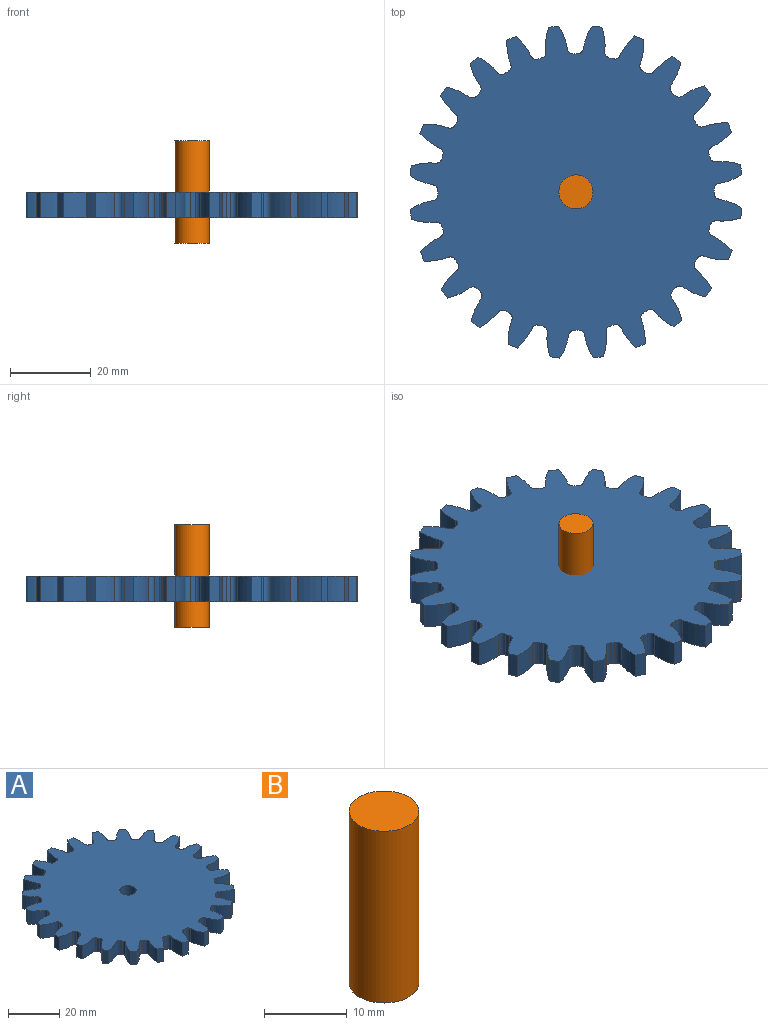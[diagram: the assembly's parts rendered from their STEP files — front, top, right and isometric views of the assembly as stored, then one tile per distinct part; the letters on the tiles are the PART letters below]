
ASSEMBLY  parts=2 mates=1
PART A: 147 faces, bbox 82.5x82.5x6.4 mm
  f0: cylinder r=3.17mm len=6.35mm, axis (0,0,1), area 126.7mm2, adj f39,f40
  f1: cylinder r=1.31mm len=6.35mm, axis (0,0,-1), area 11.8mm2, adj f39,f40,f143,f146
  f2: cylinder r=1.31mm len=6.35mm, axis (0,0,-1), area 11.8mm2, adj f39,f40,f139,f141
  f3: cylinder r=1.31mm len=6.35mm, axis (0,0,-1), area 11.8mm2, adj f39,f40,f135,f137
  f4: cylinder r=1.31mm len=6.35mm, axis (0,0,-1), area 11.8mm2, adj f39,f40,f131,f133
  f5: cylinder r=1.31mm len=6.35mm, axis (0,0,-1), area 11.8mm2, adj f39,f40,f127,f129
  f6: cylinder r=15.12mm len=6.35mm, axis (0,0,-1), area 39.4mm2, adj f21,f39,f40,f120
  f7: cylinder r=15.12mm len=6.35mm, axis (0,0,-1), area 39.4mm2, adj f31,f39,f40,f74
  f8: cylinder r=15.12mm len=6.35mm, axis (0,0,-1), area 39.4mm2, adj f32,f39,f40,f70
  f9: cylinder r=1.31mm len=6.35mm, axis (0,0,-1), area 11.8mm2, adj f39,f40,f62,f64
  f10: cylinder r=1.31mm len=6.35mm, axis (0,0,-1), area 11.8mm2, adj f39,f40,f58,f60
  f11: cylinder r=1.31mm len=6.35mm, axis (0,0,-1), area 11.8mm2, adj f39,f40,f54,f56
  f12: cylinder r=1.31mm len=6.35mm, axis (0,0,-1), area 11.8mm2, adj f39,f40,f50,f52
  f13: cylinder r=1.31mm len=6.35mm, axis (0,0,-1), area 11.8mm2, adj f39,f40,f47,f48
  f14: cylinder r=1.31mm len=6.35mm, axis (0,0,-1), area 11.8mm2, adj f39,f40,f41,f44
  f15: cylinder r=41.27mm len=6.35mm, axis (0,0,-1), area 15.7mm2, adj f39,f40,f142,f143
  f16: cylinder r=41.27mm len=6.35mm, axis (0,0,-1), area 15.7mm2, adj f39,f40,f41,f144
  f17: cylinder r=41.27mm len=6.35mm, axis (0,0,-1), area 15.7mm2, adj f39,f40,f138,f141
  f18: cylinder r=41.27mm len=6.35mm, axis (0,0,-1), area 15.7mm2, adj f39,f40,f134,f137
  f19: cylinder r=41.27mm len=6.35mm, axis (0,0,-1), area 15.7mm2, adj f39,f40,f130,f133
  f20: cylinder r=41.27mm len=6.35mm, axis (0,0,-1), area 15.7mm2, adj f39,f40,f126,f129
  f21: cylinder r=41.27mm len=6.35mm, axis (0,0,-1), area 15.7mm2, adj f6,f39,f40,f125
  f22: cylinder r=41.27mm len=6.35mm, axis (0,0,-1), area 15.7mm2, adj f39,f40,f117,f121
  f23: cylinder r=41.27mm len=6.35mm, axis (0,0,-1), area 15.7mm2, adj f39,f40,f112,f116
  f24: cylinder r=41.27mm len=6.35mm, axis (0,0,-1), area 15.7mm2, adj f39,f40,f107,f111
  f25: cylinder r=41.27mm len=6.35mm, axis (0,0,-1), area 15.7mm2, adj f39,f40,f102,f106
  f26: cylinder r=41.27mm len=6.35mm, axis (0,0,-1), area 15.7mm2, adj f39,f40,f97,f101
  f27: cylinder r=41.27mm len=6.35mm, axis (0,0,-1), area 15.7mm2, adj f39,f40,f92,f96
  f28: cylinder r=41.27mm len=6.35mm, axis (0,0,-1), area 15.7mm2, adj f39,f40,f87,f91
  f29: cylinder r=41.27mm len=6.35mm, axis (0,0,-1), area 15.7mm2, adj f39,f40,f82,f86
  f30: cylinder r=41.27mm len=6.35mm, axis (0,0,-1), area 15.7mm2, adj f39,f40,f77,f81
  f31: cylinder r=41.27mm len=6.35mm, axis (0,0,-1), area 15.7mm2, adj f7,f39,f40,f73
  f32: cylinder r=41.27mm len=6.35mm, axis (0,0,-1), area 15.7mm2, adj f8,f39,f40,f69
  f33: cylinder r=41.27mm len=6.35mm, axis (0,0,-1), area 15.7mm2, adj f39,f40,f64,f68
  f34: cylinder r=41.27mm len=6.35mm, axis (0,0,-1), area 15.7mm2, adj f39,f40,f60,f63
  f35: cylinder r=41.27mm len=6.35mm, axis (0,0,-1), area 15.7mm2, adj f39,f40,f56,f59
  f36: cylinder r=41.27mm len=6.35mm, axis (0,0,-1), area 15.7mm2, adj f39,f40,f52,f55
  f37: cylinder r=41.27mm len=6.35mm, axis (0,0,-1), area 15.7mm2, adj f39,f40,f48,f51
  f38: cylinder r=41.27mm len=6.35mm, axis (0,0,-1), area 15.7mm2, adj f39,f40,f42,f45
  f39: plane 82.53x82.53mm, normal (0,0,1), area 4433.5mm2, adj f0,f1,f2,f3,f4,f5,f6,f7
  f40: plane 82.53x82.53mm, normal (0,0,-1), area 4433.5mm2, adj f0,f1,f2,f3,f4,f5,f6,f7
  f41: cylinder r=15.12mm len=6.35mm, axis (0,0,-1), area 39.4mm2, adj f14,f16,f39,f40
  f42: cylinder r=15.12mm len=6.35mm, axis (0,0,-1), area 39.4mm2, adj f38,f39,f40,f43
  f43: cylinder r=1.31mm len=6.35mm, axis (0,0,-1), area 11.8mm2, adj f39,f40,f42,f44
  f44: cylinder r=34.24mm len=6.35mm, axis (0,0,-1), area 7.7mm2, adj f14,f39,f40,f43
  f45: cylinder r=15.12mm len=6.35mm, axis (0,0,-1), area 39.4mm2, adj f38,f39,f40,f46
  f46: cylinder r=1.31mm len=6.35mm, axis (0,0,-1), area 11.8mm2, adj f39,f40,f45,f47
  f47: cylinder r=34.24mm len=6.35mm, axis (0,0,-1), area 7.7mm2, adj f13,f39,f40,f46
  f48: cylinder r=15.12mm len=6.35mm, axis (0,0,-1), area 39.4mm2, adj f13,f37,f39,f40
  f49: cylinder r=1.31mm len=6.35mm, axis (0,0,-1), area 11.8mm2, adj f39,f40,f50,f51
  f50: cylinder r=34.24mm len=6.35mm, axis (0,0,-1), area 7.7mm2, adj f12,f39,f40,f49
  f51: cylinder r=15.12mm len=6.35mm, axis (0,0,-1), area 39.4mm2, adj f37,f39,f40,f49
  f52: cylinder r=15.12mm len=6.35mm, axis (0,0,-1), area 39.4mm2, adj f12,f36,f39,f40
  f53: cylinder r=1.31mm len=6.35mm, axis (0,0,-1), area 11.8mm2, adj f39,f40,f54,f55
  f54: cylinder r=34.24mm len=6.35mm, axis (0,0,-1), area 7.7mm2, adj f11,f39,f40,f53
  f55: cylinder r=15.12mm len=6.35mm, axis (0,0,-1), area 39.4mm2, adj f36,f39,f40,f53
  f56: cylinder r=15.12mm len=6.35mm, axis (0,0,-1), area 39.4mm2, adj f11,f35,f39,f40
  f57: cylinder r=1.31mm len=6.35mm, axis (0,0,-1), area 11.8mm2, adj f39,f40,f58,f59
  f58: cylinder r=34.24mm len=6.35mm, axis (0,0,-1), area 7.7mm2, adj f10,f39,f40,f57
  f59: cylinder r=15.12mm len=6.35mm, axis (0,0,-1), area 39.4mm2, adj f35,f39,f40,f57
  f60: cylinder r=15.12mm len=6.35mm, axis (0,0,-1), area 39.4mm2, adj f10,f34,f39,f40
  f61: cylinder r=1.31mm len=6.35mm, axis (0,0,-1), area 11.8mm2, adj f39,f40,f62,f63
  f62: cylinder r=34.24mm len=6.35mm, axis (0,0,-1), area 7.7mm2, adj f9,f39,f40,f61
  f63: cylinder r=15.12mm len=6.35mm, axis (0,0,-1), area 39.4mm2, adj f34,f39,f40,f61
  f64: cylinder r=15.12mm len=6.35mm, axis (0,0,-1), area 39.4mm2, adj f9,f33,f39,f40
  f65: cylinder r=1.31mm len=6.35mm, axis (0,0,-1), area 11.8mm2, adj f39,f40,f66,f68
  f66: cylinder r=34.24mm len=6.35mm, axis (0,0,-1), area 7.7mm2, adj f39,f40,f65,f67
  f67: cylinder r=1.31mm len=6.35mm, axis (0,0,-1), area 11.8mm2, adj f39,f40,f66,f69
  f68: cylinder r=15.12mm len=6.35mm, axis (0,0,-1), area 39.4mm2, adj f33,f39,f40,f65
  f69: cylinder r=15.12mm len=6.35mm, axis (0,0,-1), area 39.4mm2, adj f32,f39,f40,f67
  f70: cylinder r=1.31mm len=6.35mm, axis (0,0,-1), area 11.8mm2, adj f8,f39,f40,f71
  f71: cylinder r=34.24mm len=6.35mm, axis (0,0,-1), area 7.7mm2, adj f39,f40,f70,f72
  f72: cylinder r=1.31mm len=6.35mm, axis (0,0,-1), area 11.8mm2, adj f39,f40,f71,f73
  f73: cylinder r=15.12mm len=6.35mm, axis (0,0,-1), area 39.4mm2, adj f31,f39,f40,f72
  f74: cylinder r=1.31mm len=6.35mm, axis (0,0,-1), area 11.8mm2, adj f7,f39,f40,f75
  f75: cylinder r=34.24mm len=6.35mm, axis (0,0,-1), area 7.7mm2, adj f39,f40,f74,f76
  f76: cylinder r=1.31mm len=6.35mm, axis (0,0,-1), area 11.8mm2, adj f39,f40,f75,f77
  f77: cylinder r=15.12mm len=6.35mm, axis (0,0,-1), area 39.4mm2, adj f30,f39,f40,f76
  f78: cylinder r=1.31mm len=6.35mm, axis (0,0,-1), area 11.8mm2, adj f39,f40,f79,f81
  f79: cylinder r=34.24mm len=6.35mm, axis (0,0,-1), area 7.7mm2, adj f39,f40,f78,f80
  f80: cylinder r=1.31mm len=6.35mm, axis (0,0,-1), area 11.8mm2, adj f39,f40,f79,f82
  f81: cylinder r=15.12mm len=6.35mm, axis (0,0,-1), area 39.4mm2, adj f30,f39,f40,f78
  f82: cylinder r=15.12mm len=6.35mm, axis (0,0,-1), area 39.4mm2, adj f29,f39,f40,f80
  f83: cylinder r=1.31mm len=6.35mm, axis (0,0,-1), area 11.8mm2, adj f39,f40,f84,f86
  f84: cylinder r=34.24mm len=6.35mm, axis (0,0,-1), area 7.7mm2, adj f39,f40,f83,f85
  f85: cylinder r=1.31mm len=6.35mm, axis (0,0,-1), area 11.8mm2, adj f39,f40,f84,f87
  f86: cylinder r=15.12mm len=6.35mm, axis (0,0,-1), area 39.4mm2, adj f29,f39,f40,f83
  f87: cylinder r=15.12mm len=6.35mm, axis (0,0,-1), area 39.4mm2, adj f28,f39,f40,f85
  f88: cylinder r=1.31mm len=6.35mm, axis (0,0,-1), area 11.8mm2, adj f39,f40,f89,f91
  f89: cylinder r=34.24mm len=6.35mm, axis (0,0,-1), area 7.7mm2, adj f39,f40,f88,f90
  f90: cylinder r=1.31mm len=6.35mm, axis (0,0,-1), area 11.8mm2, adj f39,f40,f89,f92
  f91: cylinder r=15.12mm len=6.35mm, axis (0,0,-1), area 39.4mm2, adj f28,f39,f40,f88
  f92: cylinder r=15.12mm len=6.35mm, axis (0,0,-1), area 39.4mm2, adj f27,f39,f40,f90
  f93: cylinder r=1.31mm len=6.35mm, axis (0,0,-1), area 11.8mm2, adj f39,f40,f94,f96
  f94: cylinder r=34.24mm len=6.35mm, axis (0,0,-1), area 7.7mm2, adj f39,f40,f93,f95
  f95: cylinder r=1.31mm len=6.35mm, axis (0,0,-1), area 11.8mm2, adj f39,f40,f94,f97
  f96: cylinder r=15.12mm len=6.35mm, axis (0,0,-1), area 39.4mm2, adj f27,f39,f40,f93
  f97: cylinder r=15.12mm len=6.35mm, axis (0,0,-1), area 39.4mm2, adj f26,f39,f40,f95
  f98: cylinder r=1.31mm len=6.35mm, axis (0,0,-1), area 11.8mm2, adj f39,f40,f99,f101
  f99: cylinder r=34.24mm len=6.35mm, axis (0,0,-1), area 7.7mm2, adj f39,f40,f98,f100
  f100: cylinder r=1.31mm len=6.35mm, axis (0,0,-1), area 11.8mm2, adj f39,f40,f99,f102
  f101: cylinder r=15.12mm len=6.35mm, axis (0,0,-1), area 39.4mm2, adj f26,f39,f40,f98
  f102: cylinder r=15.12mm len=6.35mm, axis (0,0,-1), area 39.4mm2, adj f25,f39,f40,f100
  f103: cylinder r=1.31mm len=6.35mm, axis (0,0,-1), area 11.8mm2, adj f39,f40,f104,f106
  f104: cylinder r=34.24mm len=6.35mm, axis (0,0,-1), area 7.7mm2, adj f39,f40,f103,f105
  f105: cylinder r=1.31mm len=6.35mm, axis (0,0,-1), area 11.8mm2, adj f39,f40,f104,f107
  f106: cylinder r=15.12mm len=6.35mm, axis (0,0,-1), area 39.4mm2, adj f25,f39,f40,f103
  f107: cylinder r=15.12mm len=6.35mm, axis (0,0,-1), area 39.4mm2, adj f24,f39,f40,f105
  f108: cylinder r=1.31mm len=6.35mm, axis (0,0,-1), area 11.8mm2, adj f39,f40,f109,f111
  f109: cylinder r=34.24mm len=6.35mm, axis (0,0,-1), area 7.7mm2, adj f39,f40,f108,f110
  f110: cylinder r=1.31mm len=6.35mm, axis (0,0,-1), area 11.8mm2, adj f39,f40,f109,f112
  f111: cylinder r=15.12mm len=6.35mm, axis (0,0,-1), area 39.4mm2, adj f24,f39,f40,f108
  f112: cylinder r=15.12mm len=6.35mm, axis (0,0,-1), area 39.4mm2, adj f23,f39,f40,f110
  f113: cylinder r=1.31mm len=6.35mm, axis (0,0,-1), area 11.8mm2, adj f39,f40,f114,f116
  f114: cylinder r=34.24mm len=6.35mm, axis (0,0,-1), area 7.7mm2, adj f39,f40,f113,f115
  f115: cylinder r=1.31mm len=6.35mm, axis (0,0,-1), area 11.8mm2, adj f39,f40,f114,f117
  f116: cylinder r=15.12mm len=6.35mm, axis (0,0,-1), area 39.4mm2, adj f23,f39,f40,f113
  f117: cylinder r=15.12mm len=6.35mm, axis (0,0,-1), area 39.4mm2, adj f22,f39,f40,f115
  f118: cylinder r=1.31mm len=6.35mm, axis (0,0,-1), area 11.8mm2, adj f39,f40,f119,f121
  f119: cylinder r=34.24mm len=6.35mm, axis (0,0,-1), area 7.7mm2, adj f39,f40,f118,f120
  f120: cylinder r=1.31mm len=6.35mm, axis (0,0,-1), area 11.8mm2, adj f6,f39,f40,f119
  f121: cylinder r=15.12mm len=6.35mm, axis (0,0,-1), area 39.4mm2, adj f22,f39,f40,f118
  f122: cylinder r=1.31mm len=6.35mm, axis (0,0,-1), area 11.8mm2, adj f39,f40,f123,f125
  f123: cylinder r=34.24mm len=6.35mm, axis (0,0,-1), area 7.7mm2, adj f39,f40,f122,f124
  f124: cylinder r=1.31mm len=6.35mm, axis (0,0,-1), area 11.8mm2, adj f39,f40,f123,f126
  f125: cylinder r=15.12mm len=6.35mm, axis (0,0,-1), area 39.4mm2, adj f21,f39,f40,f122
  f126: cylinder r=15.12mm len=6.35mm, axis (0,0,-1), area 39.4mm2, adj f20,f39,f40,f124
  f127: cylinder r=34.24mm len=6.35mm, axis (0,0,-1), area 7.7mm2, adj f5,f39,f40,f128
  f128: cylinder r=1.31mm len=6.35mm, axis (0,0,-1), area 11.8mm2, adj f39,f40,f127,f130
  f129: cylinder r=15.12mm len=6.35mm, axis (0,0,-1), area 39.4mm2, adj f5,f20,f39,f40
  f130: cylinder r=15.12mm len=6.35mm, axis (0,0,-1), area 39.4mm2, adj f19,f39,f40,f128
  f131: cylinder r=34.24mm len=6.35mm, axis (0,0,-1), area 7.7mm2, adj f4,f39,f40,f132
  f132: cylinder r=1.31mm len=6.35mm, axis (0,0,-1), area 11.8mm2, adj f39,f40,f131,f134
  f133: cylinder r=15.12mm len=6.35mm, axis (0,0,-1), area 39.4mm2, adj f4,f19,f39,f40
  f134: cylinder r=15.12mm len=6.35mm, axis (0,0,-1), area 39.4mm2, adj f18,f39,f40,f132
  f135: cylinder r=34.24mm len=6.35mm, axis (0,0,-1), area 7.7mm2, adj f3,f39,f40,f136
  f136: cylinder r=1.31mm len=6.35mm, axis (0,0,-1), area 11.8mm2, adj f39,f40,f135,f138
  f137: cylinder r=15.12mm len=6.35mm, axis (0,0,-1), area 39.4mm2, adj f3,f18,f39,f40
  f138: cylinder r=15.12mm len=6.35mm, axis (0,0,-1), area 39.4mm2, adj f17,f39,f40,f136
  f139: cylinder r=34.24mm len=6.35mm, axis (0,0,-1), area 7.7mm2, adj f2,f39,f40,f140
  f140: cylinder r=1.31mm len=6.35mm, axis (0,0,-1), area 11.8mm2, adj f39,f40,f139,f142
  f141: cylinder r=15.12mm len=6.35mm, axis (0,0,-1), area 39.4mm2, adj f2,f17,f39,f40
  f142: cylinder r=15.12mm len=6.35mm, axis (0,0,-1), area 39.4mm2, adj f15,f39,f40,f140
  f143: cylinder r=15.12mm len=6.35mm, axis (0,0,-1), area 39.4mm2, adj f1,f15,f39,f40
  f144: cylinder r=15.12mm len=6.35mm, axis (0,0,-1), area 39.4mm2, adj f16,f39,f40,f145
  f145: cylinder r=1.31mm len=6.35mm, axis (0,0,-1), area 11.8mm2, adj f39,f40,f144,f146
  f146: cylinder r=34.24mm len=6.35mm, axis (0,0,-1), area 7.7mm2, adj f1,f39,f40,f145
PART B: 3 faces, bbox 8.4x8.4x25.4 mm
  f0: cylinder r=4.22mm len=25.4mm, axis (0,0,-1), area 673.2mm2, adj f1,f2
  f1: plane 8.44x8.44mm, normal (0,0,1), area 55.9mm2, adj f0
  f2: plane 8.44x8.44mm, normal (0,0,-1), area 55.9mm2, adj f0
PLACE A rot(axis=(0,0,-1),10.1deg) t=(-80.1,-6.92,12.7)mm
PLACE B at identity fixed
MATE revolute B.f0 <-> A.f0  axis (0,0,-1) through (-80.1,-6.92,6.35)mm
